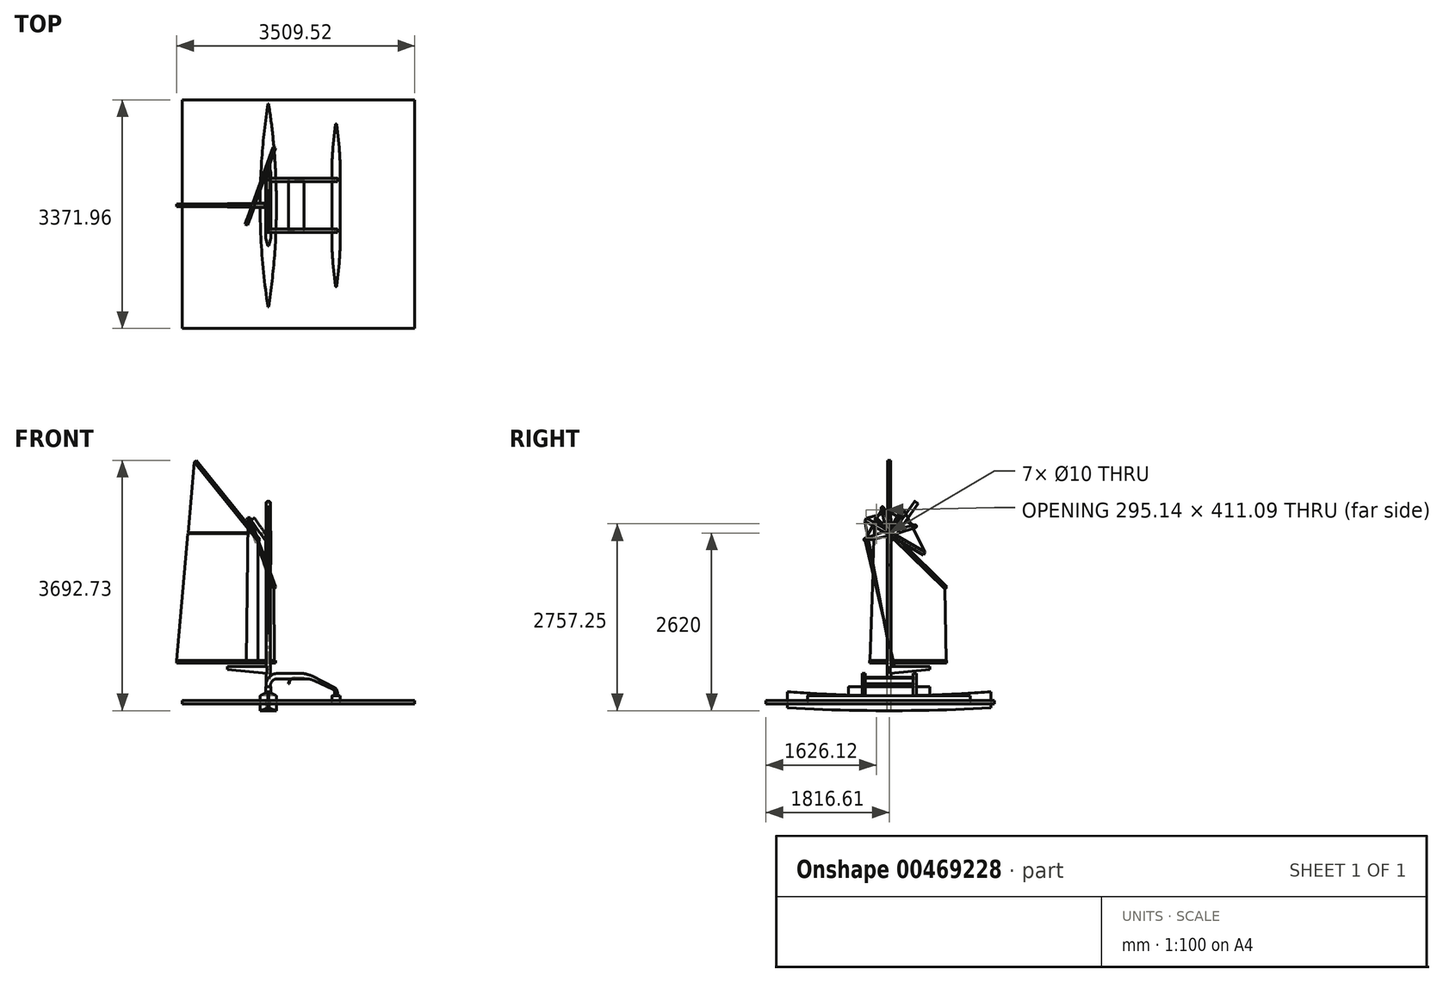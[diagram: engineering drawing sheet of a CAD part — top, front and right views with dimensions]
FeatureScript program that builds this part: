
annotation { "Feature Type Name" : "Feature", "Feature Type Description" : "" }
export const myFeature = defineFeature(function(context is Context, id is Id, definition is map)
    precondition{}
    {
        {
            var Q0;
            Q0=qCreatedBy(makeId("Top.planeOp"),FACE);
            var sketch = newSketch(context, id + "F0", { "sketchPlane" : qUnion([Q0])});
            skLineSegment(sketch, "E0", {"start": v(0, 0) * mm, "end": v(0, 1500) * mm});
            skLineSegment(sketch, "E1", {"start": v(0, 0) * mm, "end": v(120, 0) * mm});
            skLineSegment(sketch, "E2", {"start": v(120, 0) * mm, "end": v(120, -200) * mm, "construction": true});
            skLineSegment(sketch, "E3", {"start": v(0, 1500) * mm, "end": v(5, 1500) * mm});
            skArc(sketch, "E4", {"start": v(120, 0) * mm, "mid": v(91.2, 752.2) * mm, "end": v(5, 1500) * mm});
            skSolve(sketch);
        }
        {
            var Q0;
            Q0=qSketchRegion(id+"F0",true);
            extrude(context, id + "F1", {"entities" : qUnion([Q0]), "depth" : 110 * mm});
        }
        {
            var Q0;
            Q0=qCreatedBy(makeId("Right.planeOp"),FACE);
            var sketch = newSketch(context, id + "F2", { "sketchPlane" : qUnion([Q0])});
            skLineSegment(sketch, "E5.0", {"start": v(0, 0) * mm, "end": v(1500, 0) * mm});
            skLineSegment(sketch, "E6", {"start": v(1500, 0) * mm, "end": v(1500, 40) * mm});
            skLineSegment(sketch, "E7", {"start": v(0, 0) * mm, "end": v(-216.61, 0) * mm, "construction": true});
            skArc(sketch, "E8", {"start": v(0, 0) * mm, "mid": v(750.27, 10) * mm, "end": v(1500, 40) * mm});
            skSolve(sketch);
        }
        {
            var Q0;
            Q0=qSketchRegion(id+"F2",true);
            extrude(context, id + "F3", {"entities" : qUnion([Q0]), "operationType" : NewBodyOperationType.REMOVE, "depth" : 200 * mm});
        }
        {
            var Q0;
            Q0=makeQuery(id+"F1.opExtrude","SWEPT_BODY",BODY,{"disambiguationData":[OSD([sQuery(id+"F0.wireOp",EDGE,"E0"),sQuery(id+"F0.wireOp",EDGE,"E1"),sQuery(id+"F0.wireOp",EDGE,"E3"),sQuery(id+"F0.wireOp",EDGE,"E4")])]});
            var Q1;
            Q1=makeQuery(id+"F1.opExtrude","CAP_FACE",FACE,{"disambiguationData":[OSD([sQuery(id+"F0.wireOp",EDGE,"E0"),sQuery(id+"F0.wireOp",EDGE,"E1"),sQuery(id+"F0.wireOp",EDGE,"E3"),sQuery(id+"F0.wireOp",EDGE,"E4")])],"isStart":false});
            mirror(context, id + "F4", {"operationType" : NewBodyOperationType.ADD, "entities" : qUnion([Q0]), "mirrorPlane" : qUnion([Q1])});
        }
        {
            var Q0;
            Q0=makeQuery(id+"F1.opExtrude","SWEPT_BODY",BODY,{"disambiguationData":[OSD([sQuery(id+"F0.wireOp",EDGE,"E0"),sQuery(id+"F0.wireOp",EDGE,"E1"),sQuery(id+"F0.wireOp",EDGE,"E3"),sQuery(id+"F0.wireOp",EDGE,"E4")])]});
            var Q1;
            Q1=qCreatedBy(makeId("Right.planeOp"),FACE);
            mirror(context, id + "F5", {"operationType" : NewBodyOperationType.ADD, "entities" : qUnion([Q0]), "mirrorPlane" : qUnion([Q1])});
        }
        {
            var Q0;
            Q0=makeQuery(id+"F1.opExtrude","SWEPT_BODY",BODY,{"disambiguationData":[OSD([sQuery(id+"F0.wireOp",EDGE,"E0"),sQuery(id+"F0.wireOp",EDGE,"E1"),sQuery(id+"F0.wireOp",EDGE,"E3"),sQuery(id+"F0.wireOp",EDGE,"E4")])]});
            var Q1;
            Q1=qCreatedBy(makeId("Front.planeOp"),FACE);
            mirror(context, id + "F6", {"operationType" : NewBodyOperationType.ADD, "entities" : qUnion([Q0]), "mirrorPlane" : qUnion([Q1])});
        }
        {
            var Q0;
            Q0=qCreatedBy(makeId("Right.planeOp"),FACE);
            var sketch = newSketch(context, id + "F7", { "sketchPlane" : qUnion([Q0])});
            skLineSegment(sketch, "E9", {"start": v(-1500, 180) * mm, "end": v(-1500, 280) * mm});
            skLineSegment(sketch, "E10", {"start": v(1500, 180) * mm, "end": v(1500, 280) * mm});
            skLineSegment(sketch, "E11", {"start": v(0, 0) * mm, "end": v(0, 220) * mm, "construction": true});
            skArc(sketch, "E12", {"start": v(-1500, 280) * mm, "mid": v(0, 220) * mm, "end": v(1500, 280) * mm});
            skLineSegment(sketch, "E13", {"start": v(-1500, 180) * mm, "end": v(1500, 180) * mm});
            skSolve(sketch);
        }
        {
            var Q0;
            Q0=qSketchRegion(id+"F7",true);
            extrude(context, id + "F8", {"entities" : qUnion([Q0]), "operationType" : NewBodyOperationType.ADD, "depth" : 200 * mm, "hasSecondDirection" : true, "secondDirectionOppositeDirection" : true, "secondDirectionDepth" : 200 * mm});
        }
        {
            var Q0;
            Q0=makeQuery(id+"F8.opExtrude","SWEPT_FACE",FACE,{"disambiguationData":[OSD([sQuery(id+"F7.wireOp",EDGE,"E13")])]});
            var sketch = newSketch(context, id + "F9", { "sketchPlane" : qUnion([Q0])});
            skLineSegment(sketch, "E14.0", {"start": v(200, 1500) * mm, "end": v(200, -1500) * mm});
            skLineSegment(sketch, "E15.0", {"start": v(5, -1500) * mm, "end": v(-5, -1500) * mm});
            skLineSegment(sketch, "E16.0", {"start": v(-200, 1500) * mm, "end": v(-200, -1500) * mm});
            skArc(sketch, "E17.0", {"start": v(5, -1500) * mm, "mid": v(120, 0) * mm, "end": v(5, 1500) * mm});
            skArc(sketch, "E18.0", {"start": v(-5, 1500) * mm, "mid": v(-120, 0) * mm, "end": v(-5, -1500) * mm});
            skLineSegment(sketch, "E19.0", {"start": v(5, 1500) * mm, "end": v(-5, 1500) * mm});
            skLineSegment(sketch, "E20", {"start": v(-200, 1500) * mm, "end": v(-200, 1658.3) * mm});
            skLineSegment(sketch, "E21", {"start": v(-200, 1658.3) * mm, "end": v(200, 1658.3) * mm});
            skLineSegment(sketch, "E22", {"start": v(200, 1500) * mm, "end": v(200, 1658.3) * mm});
            skPoint(sketch, "E23.orphan", {"position": v(211.73, 1658.3) * mm});
            skLineSegment(sketch, "E24", {"start": v(-200, -1500) * mm, "end": v(-200, -1609.33) * mm});
            skLineSegment(sketch, "E25", {"start": v(200, -1500) * mm, "end": v(200, -1609.33) * mm});
            skLineSegment(sketch, "E26", {"start": v(-200, -1609.33) * mm, "end": v(200, -1609.33) * mm});
            skSolve(sketch);
        }
        {
            var Q0;
            Q0=qSketchRegion(id+"F9",true);
            extrude(context, id + "F10", {"entities" : qUnion([Q0]), "operationType" : NewBodyOperationType.REMOVE, "oppositeDirection" : true, "depth" : 200 * mm});
        }
        {
            var Q0;
            Q0=qCreatedBy(makeId("Top.planeOp"),FACE);
            cPlane(context, id + "F11", {"entities" : qUnion([Q0]), "cplaneType" : CPlaneType.OFFSET, "offset" : 100 * mm, "width" : 150 * mm, "height" : 150 * mm});
        }
        {
            var Q0;
            Q0=qCreatedBy(id+"F11.planeOp",FACE);
            var sketch = newSketch(context, id + "F12", { "sketchPlane" : qUnion([Q0])});
            skLineSegment(sketch, "E27.bottom", {"start": v(40, -600) * mm, "end": v(-40, -600) * mm});
            skLineSegment(sketch, "E27.top", {"start": v(40, 600) * mm, "end": v(-40, 600) * mm});
            skLineSegment(sketch, "E27.left", {"start": v(40, -600) * mm, "end": v(40, 600) * mm});
            skLineSegment(sketch, "E27.right", {"start": v(-40, -600) * mm, "end": v(-40, 600) * mm});
            skPoint(sketch, "E27.middle", {"position": v(0, 0) * mm});
            skSolve(sketch);
        }
        {
            var Q0;
            Q0=qSketchRegion(id+"F12",true);
            extrude(context, id + "F13", {"entities" : qUnion([Q0]), "operationType" : NewBodyOperationType.ADD, "depth" : 250 * mm});
        }
        {
            var Q0;
            Q0=makeQuery(id+"F13.opExtrude","SWEPT_EDGE",EDGE,{"disambiguationData":[OSD([sQuery(id+"F12.wireOp",EDGE,"E27.bottom"),sQuery(id+"F12.wireOp",EDGE,"E27.left")])]});
            var Q1;
            Q1=makeQuery(id+"F13.opExtrude","SWEPT_EDGE",EDGE,{"disambiguationData":[OSD([sQuery(id+"F12.wireOp",EDGE,"E27.bottom"),sQuery(id+"F12.wireOp",EDGE,"E27.right")])]});
            var Q2;
            Q2=makeQuery(id+"F13.opExtrude","SWEPT_EDGE",EDGE,{"disambiguationData":[OSD([sQuery(id+"F12.wireOp",EDGE,"E27.top"),sQuery(id+"F12.wireOp",EDGE,"E27.right")])]});
            var Q3;
            Q3=makeQuery(id+"F13.opExtrude","SWEPT_EDGE",EDGE,{"disambiguationData":[OSD([sQuery(id+"F12.wireOp",EDGE,"E27.top"),sQuery(id+"F12.wireOp",EDGE,"E27.left")])]});
            chamfer(context, id + "F14", {"entities" : qUnion([Q0, Q1, Q2, Q3]), "chamferType" : ChamferType.TWO_OFFSETS, "width1" : 35 * mm, "oppositeDirection" : true, "width2" : 120 * mm, "tangentPropagation" : true});
        }
        {
            var Q0;
            {var subQ0=sQuery(id+"F12.wireOp",EDGE,"E27.top");Q0=makeQuery(id+"F14.opChamfer","BLEND_EDGE",EDGE,{"blendedFrom":[makeQuery(id+"F13.opExtrude","SWEPT_EDGE",EDGE,{"disambiguationData":[OSD([subQ0,sQuery(id+"F12.wireOp",EDGE,"E27.right")])]}),makeQuery(id+"F13.opExtrude","SWEPT_FACE",FACE,{"disambiguationData":[OSD([subQ0])]})],"blendedInto":[makeQuery(id+"F13.opExtrude","SWEPT_FACE",FACE,{"disambiguationData":[OSD([subQ0])]})]});}
            var Q1;
            {var subQ0=sQuery(id+"F12.wireOp",EDGE,"E27.top");Q1=makeQuery(id+"F14.opChamfer","BLEND_EDGE",EDGE,{"blendedFrom":[makeQuery(id+"F13.opExtrude","SWEPT_EDGE",EDGE,{"disambiguationData":[OSD([subQ0,sQuery(id+"F12.wireOp",EDGE,"E27.left")])]}),makeQuery(id+"F13.opExtrude","SWEPT_FACE",FACE,{"disambiguationData":[OSD([subQ0])]})],"blendedInto":[makeQuery(id+"F13.opExtrude","SWEPT_FACE",FACE,{"disambiguationData":[OSD([subQ0])]})]});}
            var Q2;
            {var subQ0=sQuery(id+"F12.wireOp",EDGE,"E27.bottom");Q2=makeQuery(id+"F14.opChamfer","BLEND_EDGE",EDGE,{"blendedFrom":[makeQuery(id+"F13.opExtrude","SWEPT_EDGE",EDGE,{"disambiguationData":[OSD([subQ0,sQuery(id+"F12.wireOp",EDGE,"E27.right")])]}),makeQuery(id+"F13.opExtrude","SWEPT_FACE",FACE,{"disambiguationData":[OSD([subQ0])]})],"blendedInto":[makeQuery(id+"F13.opExtrude","SWEPT_FACE",FACE,{"disambiguationData":[OSD([subQ0])]})]});}
            var Q3;
            {var subQ0=sQuery(id+"F12.wireOp",EDGE,"E27.bottom");Q3=makeQuery(id+"F14.opChamfer","BLEND_EDGE",EDGE,{"blendedFrom":[makeQuery(id+"F13.opExtrude","SWEPT_EDGE",EDGE,{"disambiguationData":[OSD([subQ0,sQuery(id+"F12.wireOp",EDGE,"E27.left")])]}),makeQuery(id+"F13.opExtrude","SWEPT_FACE",FACE,{"disambiguationData":[OSD([subQ0])]})],"blendedInto":[makeQuery(id+"F13.opExtrude","SWEPT_FACE",FACE,{"disambiguationData":[OSD([subQ0])]})]});}
            fillet(context, id + "F15", {"entities" : qUnion([Q0, Q1, Q2, Q3]), "radius" : 5 * mm, "tangentPropagation" : true, "allowEdgeOverflow" : false});
        }
        {
            var Q0;
            {var subQ0=sQuery(id+"F12.wireOp",EDGE,"E27.right");Q0=makeQuery(id+"F14.opChamfer","BLEND_EDGE",EDGE,{"blendedFrom":[makeQuery(id+"F13.opExtrude","SWEPT_EDGE",EDGE,{"disambiguationData":[OSD([sQuery(id+"F12.wireOp",EDGE,"E27.bottom"),subQ0])]}),makeQuery(id+"F13.opExtrude","SWEPT_FACE",FACE,{"disambiguationData":[OSD([subQ0])]})],"blendedInto":[makeQuery(id+"F13.opExtrude","SWEPT_FACE",FACE,{"disambiguationData":[OSD([subQ0])]})]});}
            var Q1;
            {var subQ0=sQuery(id+"F12.wireOp",EDGE,"E27.left");Q1=makeQuery(id+"F14.opChamfer","BLEND_EDGE",EDGE,{"blendedFrom":[makeQuery(id+"F13.opExtrude","SWEPT_EDGE",EDGE,{"disambiguationData":[OSD([sQuery(id+"F12.wireOp",EDGE,"E27.bottom"),subQ0])]}),makeQuery(id+"F13.opExtrude","SWEPT_FACE",FACE,{"disambiguationData":[OSD([subQ0])]})],"blendedInto":[makeQuery(id+"F13.opExtrude","SWEPT_FACE",FACE,{"disambiguationData":[OSD([subQ0])]})]});}
            var Q2;
            {var subQ0=sQuery(id+"F12.wireOp",EDGE,"E27.left");Q2=makeQuery(id+"F14.opChamfer","BLEND_EDGE",EDGE,{"blendedFrom":[makeQuery(id+"F13.opExtrude","SWEPT_EDGE",EDGE,{"disambiguationData":[OSD([sQuery(id+"F12.wireOp",EDGE,"E27.top"),subQ0])]}),makeQuery(id+"F13.opExtrude","SWEPT_FACE",FACE,{"disambiguationData":[OSD([subQ0])]})],"blendedInto":[makeQuery(id+"F13.opExtrude","SWEPT_FACE",FACE,{"disambiguationData":[OSD([subQ0])]})]});}
            var Q3;
            {var subQ0=sQuery(id+"F12.wireOp",EDGE,"E27.right");Q3=makeQuery(id+"F14.opChamfer","BLEND_EDGE",EDGE,{"blendedFrom":[makeQuery(id+"F13.opExtrude","SWEPT_EDGE",EDGE,{"disambiguationData":[OSD([sQuery(id+"F12.wireOp",EDGE,"E27.top"),subQ0])]}),makeQuery(id+"F13.opExtrude","SWEPT_FACE",FACE,{"disambiguationData":[OSD([subQ0])]})],"blendedInto":[makeQuery(id+"F13.opExtrude","SWEPT_FACE",FACE,{"disambiguationData":[OSD([subQ0])]})]});}
            fillet(context, id + "F16", {"entities" : qUnion([Q0, Q1, Q2, Q3]), "radius" : 200 * mm, "tangentPropagation" : true, "allowEdgeOverflow" : false});
        }
        {
            var Q0;
            Q0=qCreatedBy(id+"F11.planeOp",FACE);
            var sketch = newSketch(context, id + "F17", { "sketchPlane" : qUnion([Q0])});
            skLineSegment(sketch, "E28.bottom", {"start": v(1060, 1200) * mm, "end": v(940, 1200) * mm});
            skLineSegment(sketch, "E28.top", {"start": v(1060, -1200) * mm, "end": v(940, -1200) * mm});
            skLineSegment(sketch, "E28.left", {"start": v(1060, 1200) * mm, "end": v(1060, -1200) * mm});
            skLineSegment(sketch, "E28.right", {"start": v(940, 1200) * mm, "end": v(940, -1200) * mm});
            skPoint(sketch, "E28.middle", {"position": v(1000, 0) * mm});
            skSolve(sketch);
        }
        {
            var Q0;
            Q0=qSketchRegion(id+"F17",true);
            extrude(context, id + "F18", {"entities" : qUnion([Q0]), "depth" : 120 * mm});
        }
        {
            var Q0;
            Q0=makeQuery(id+"F18.opExtrude","SWEPT_EDGE",EDGE,{"disambiguationData":[OSD([sQuery(id+"F17.wireOp",EDGE,"E28.top"),sQuery(id+"F17.wireOp",EDGE,"E28.right")])]});
            var Q1;
            Q1=makeQuery(id+"F18.opExtrude","SWEPT_EDGE",EDGE,{"disambiguationData":[OSD([sQuery(id+"F17.wireOp",EDGE,"E28.top"),sQuery(id+"F17.wireOp",EDGE,"E28.left")])]});
            var Q2;
            Q2=makeQuery(id+"F18.opExtrude","SWEPT_EDGE",EDGE,{"disambiguationData":[OSD([sQuery(id+"F17.wireOp",EDGE,"E28.bottom"),sQuery(id+"F17.wireOp",EDGE,"E28.right")])]});
            var Q3;
            Q3=makeQuery(id+"F18.opExtrude","SWEPT_EDGE",EDGE,{"disambiguationData":[OSD([sQuery(id+"F17.wireOp",EDGE,"E28.bottom"),sQuery(id+"F17.wireOp",EDGE,"E28.left")])]});
            chamfer(context, id + "F19", {"entities" : qUnion([Q0, Q1, Q2, Q3]), "chamferType" : ChamferType.TWO_OFFSETS, "width1" : 50 * mm, "oppositeDirection" : false, "width2" : 500 * mm, "tangentPropagation" : true});
        }
        {
            var Q0;
            {var subQ0=sQuery(id+"F17.wireOp",EDGE,"E28.top");Q0=makeQuery(id+"F19.opChamfer","BLEND_EDGE",EDGE,{"blendedFrom":[makeQuery(id+"F18.opExtrude","SWEPT_EDGE",EDGE,{"disambiguationData":[OSD([subQ0,sQuery(id+"F17.wireOp",EDGE,"E28.right")])]}),makeQuery(id+"F18.opExtrude","SWEPT_FACE",FACE,{"disambiguationData":[OSD([subQ0])]})],"blendedInto":[makeQuery(id+"F18.opExtrude","SWEPT_FACE",FACE,{"disambiguationData":[OSD([subQ0])]})]});}
            var Q1;
            {var subQ0=sQuery(id+"F17.wireOp",EDGE,"E28.top");Q1=makeQuery(id+"F19.opChamfer","BLEND_EDGE",EDGE,{"blendedFrom":[makeQuery(id+"F18.opExtrude","SWEPT_EDGE",EDGE,{"disambiguationData":[OSD([subQ0,sQuery(id+"F17.wireOp",EDGE,"E28.left")])]}),makeQuery(id+"F18.opExtrude","SWEPT_FACE",FACE,{"disambiguationData":[OSD([subQ0])]})],"blendedInto":[makeQuery(id+"F18.opExtrude","SWEPT_FACE",FACE,{"disambiguationData":[OSD([subQ0])]})]});}
            var Q2;
            {var subQ0=sQuery(id+"F17.wireOp",EDGE,"E28.bottom");Q2=makeQuery(id+"F19.opChamfer","BLEND_EDGE",EDGE,{"blendedFrom":[makeQuery(id+"F18.opExtrude","SWEPT_EDGE",EDGE,{"disambiguationData":[OSD([subQ0,sQuery(id+"F17.wireOp",EDGE,"E28.right")])]}),makeQuery(id+"F18.opExtrude","SWEPT_FACE",FACE,{"disambiguationData":[OSD([subQ0])]})],"blendedInto":[makeQuery(id+"F18.opExtrude","SWEPT_FACE",FACE,{"disambiguationData":[OSD([subQ0])]})]});}
            var Q3;
            {var subQ0=sQuery(id+"F17.wireOp",EDGE,"E28.bottom");Q3=makeQuery(id+"F19.opChamfer","BLEND_EDGE",EDGE,{"blendedFrom":[makeQuery(id+"F18.opExtrude","SWEPT_EDGE",EDGE,{"disambiguationData":[OSD([subQ0,sQuery(id+"F17.wireOp",EDGE,"E28.left")])]}),makeQuery(id+"F18.opExtrude","SWEPT_FACE",FACE,{"disambiguationData":[OSD([subQ0])]})],"blendedInto":[makeQuery(id+"F18.opExtrude","SWEPT_FACE",FACE,{"disambiguationData":[OSD([subQ0])]})]});}
            fillet(context, id + "F20", {"entities" : qUnion([Q0, Q1, Q2, Q3]), "radius" : 10 * mm, "tangentPropagation" : true, "allowEdgeOverflow" : false});
        }
        {
            var Q0;
            {var subQ0=sQuery(id+"F17.wireOp",EDGE,"E28.left");Q0=makeQuery(id+"F19.opChamfer","BLEND_EDGE",EDGE,{"blendedFrom":[makeQuery(id+"F18.opExtrude","SWEPT_EDGE",EDGE,{"disambiguationData":[OSD([sQuery(id+"F17.wireOp",EDGE,"E28.bottom"),subQ0])]}),makeQuery(id+"F18.opExtrude","SWEPT_FACE",FACE,{"disambiguationData":[OSD([subQ0])]})],"blendedInto":[makeQuery(id+"F18.opExtrude","SWEPT_FACE",FACE,{"disambiguationData":[OSD([subQ0])]})]});}
            var Q1;
            {var subQ0=sQuery(id+"F17.wireOp",EDGE,"E28.right");Q1=makeQuery(id+"F19.opChamfer","BLEND_EDGE",EDGE,{"blendedFrom":[makeQuery(id+"F18.opExtrude","SWEPT_EDGE",EDGE,{"disambiguationData":[OSD([sQuery(id+"F17.wireOp",EDGE,"E28.bottom"),subQ0])]}),makeQuery(id+"F18.opExtrude","SWEPT_FACE",FACE,{"disambiguationData":[OSD([subQ0])]})],"blendedInto":[makeQuery(id+"F18.opExtrude","SWEPT_FACE",FACE,{"disambiguationData":[OSD([subQ0])]})]});}
            var Q2;
            {var subQ0=sQuery(id+"F17.wireOp",EDGE,"E28.right");Q2=makeQuery(id+"F19.opChamfer","BLEND_EDGE",EDGE,{"blendedFrom":[makeQuery(id+"F18.opExtrude","SWEPT_EDGE",EDGE,{"disambiguationData":[OSD([sQuery(id+"F17.wireOp",EDGE,"E28.top"),subQ0])]}),makeQuery(id+"F18.opExtrude","SWEPT_FACE",FACE,{"disambiguationData":[OSD([subQ0])]})],"blendedInto":[makeQuery(id+"F18.opExtrude","SWEPT_FACE",FACE,{"disambiguationData":[OSD([subQ0])]})]});}
            var Q3;
            {var subQ0=sQuery(id+"F17.wireOp",EDGE,"E28.left");Q3=makeQuery(id+"F19.opChamfer","BLEND_EDGE",EDGE,{"blendedFrom":[makeQuery(id+"F18.opExtrude","SWEPT_EDGE",EDGE,{"disambiguationData":[OSD([sQuery(id+"F17.wireOp",EDGE,"E28.top"),subQ0])]}),makeQuery(id+"F18.opExtrude","SWEPT_FACE",FACE,{"disambiguationData":[OSD([subQ0])]})],"blendedInto":[makeQuery(id+"F18.opExtrude","SWEPT_FACE",FACE,{"disambiguationData":[OSD([subQ0])]})]});}
            fillet(context, id + "F21", {"entities" : qUnion([Q0, Q1, Q2, Q3]), "radius" : 3000 * mm, "tangentPropagation" : true, "allowEdgeOverflow" : false});
        }
        {
            var Q0;
            Q0=qCreatedBy(makeId("Front.planeOp"),FACE);
            cPlane(context, id + "F22", {"entities" : qUnion([Q0]), "cplaneType" : CPlaneType.OFFSET, "offset" : 400 * mm, "width" : 150 * mm, "height" : 150 * mm});
        }
        {
            var Q0;
            Q0=qCreatedBy(id+"F22.planeOp",FACE);
            var sketch = newSketch(context, id + "F23", { "sketchPlane" : qUnion([Q0])});
            skLineSegment(sketch, "E29", {"start": v(33.27, 350) * mm, "end": v(-33.27, 350) * mm});
            skLineSegment(sketch, "E30", {"start": v(1020, 220) * mm, "end": v(980, 220) * mm});
            skLineSegment(sketch, "E31", {"start": v(-33.27, 350) * mm, "end": v(-33.27, 380) * mm});
            skLineSegment(sketch, "E32", {"start": v(136.73, 550) * mm, "end": v(475.83, 550) * mm});
            skLineSegment(sketch, "E33", {"start": v(33.27, 350) * mm, "end": v(33.27, 370) * mm});
            skLineSegment(sketch, "E34", {"start": v(980, 220) * mm, "end": v(980, 268.3) * mm});
            skLineSegment(sketch, "E35", {"start": v(1020, 220) * mm, "end": v(1020, 270.88) * mm});
            skPoint(sketch, "E36.orphan", {"position": v(1060, 220) * mm});
            skPoint(sketch, "E37.orphan", {"position": v(940, 220) * mm});
            skLineSegment(sketch, "E38", {"start": v(647.78, 508.87) * mm, "end": v(976.2, 342.23) * mm});
            skLineSegment(sketch, "E39", {"start": v(133.27, 470) * mm, "end": v(552.25, 470) * mm});
            skLineSegment(sketch, "E40", {"start": v(680.18, 441.35) * mm, "end": v(951.32, 313.52) * mm});
            skPoint(sketch, "E41.visualSharp", {"position": v(33.27, 470) * mm});
            skArc(sketch, "E41.filletArc", {"start": v(133.27, 470) * mm, "mid": v(62.56, 440.71) * mm, "end": v(33.27, 370) * mm});
            skPoint(sketch, "E42.visualSharp", {"position": v(-33.27, 550) * mm});
            skArc(sketch, "E42.filletArc", {"start": v(136.73, 550) * mm, "mid": v(16.52, 500.2) * mm, "end": v(-33.27, 380) * mm});
            skPoint(sketch, "E43.visualSharp", {"position": v(619.42, 470) * mm});
            skArc(sketch, "E43.filletArc", {"start": v(680.18, 441.35) * mm, "mid": v(617.8, 462.75) * mm, "end": v(552.25, 470) * mm});
            skPoint(sketch, "E44.visualSharp", {"position": v(566.73, 550) * mm});
            skArc(sketch, "E44.filletArc", {"start": v(647.78, 508.87) * mm, "mid": v(564.23, 539.57) * mm, "end": v(475.83, 550) * mm});
            skPoint(sketch, "E45.visualSharp", {"position": v(980, 300) * mm});
            skArc(sketch, "E45.filletArc", {"start": v(980, 268.3) * mm, "mid": v(972.23, 295.07) * mm, "end": v(951.32, 313.52) * mm});
            skPoint(sketch, "E46.visualSharp", {"position": v(1020, 320) * mm});
            skArc(sketch, "E46.filletArc", {"start": v(1020, 270.88) * mm, "mid": v(1008.18, 312.74) * mm, "end": v(976.2, 342.23) * mm});
            skSolve(sketch);
        }
        {
            var Q0;
            Q0=qSketchRegion(id+"F23",true);
            extrude(context, id + "F24", {"entities" : qUnion([Q0]), "oppositeDirection" : true, "depth" : 50 * mm});
        }
        {
            var Q0;
            Q0=makeQuery(id+"F24.opExtrude","SWEPT_BODY",BODY,{"disambiguationData":[OSD([sQuery(id+"F23.wireOp",EDGE,"E29"),sQuery(id+"F23.wireOp",EDGE,"E30"),sQuery(id+"F23.wireOp",EDGE,"E31"),sQuery(id+"F23.wireOp",EDGE,"E32"),sQuery(id+"F23.wireOp",EDGE,"E33"),sQuery(id+"F23.wireOp",EDGE,"E34"),sQuery(id+"F23.wireOp",EDGE,"E35"),sQuery(id+"F23.wireOp",EDGE,"E38"),sQuery(id+"F23.wireOp",EDGE,"E39"),sQuery(id+"F23.wireOp",EDGE,"E40"),sQuery(id+"F23.wireOp",EDGE,"E41.filletArc"),sQuery(id+"F23.wireOp",EDGE,"E42.filletArc"),sQuery(id+"F23.wireOp",EDGE,"E43.filletArc"),sQuery(id+"F23.wireOp",EDGE,"E44.filletArc"),sQuery(id+"F23.wireOp",EDGE,"E45.filletArc"),sQuery(id+"F23.wireOp",EDGE,"E46.filletArc")])]});
            var Q1;
            Q1=qCreatedBy(makeId("Front.planeOp"),FACE);
            mirror(context, id + "F25", {"entities" : qUnion([Q0]), "mirrorPlane" : qUnion([Q1])});
        }
        {
            var Q0;
            Q0=qCreatedBy(makeId("Front.planeOp"),FACE);
            var sketch = newSketch(context, id + "F26", { "sketchPlane" : qUnion([Q0])});
            skLineSegment(sketch, "E47", {"start": v(0, 0) * mm, "end": v(0, 2500) * mm});
            skLineSegment(sketch, "E48", {"start": v(0, 2500) * mm, "end": v(-229.43, 2827.66) * mm});
            skPoint(sketch, "E49.visualSharp", {"position": v(0, 2500) * mm});
            skSolve(sketch);
        }
        {
            var Q0;
            Q0=makeQuery(id+"F13.opExtrude","CAP_FACE",FACE,{"disambiguationData":[OSD([sQuery(id+"F12.wireOp",EDGE,"E27.bottom"),sQuery(id+"F12.wireOp",EDGE,"E27.top"),sQuery(id+"F12.wireOp",EDGE,"E27.left"),sQuery(id+"F12.wireOp",EDGE,"E27.right")])],"isStart":false});
            var sketch = newSketch(context, id + "F27", { "sketchPlane" : qUnion([Q0])});
            skCircle(sketch, "E50", {"center": v(0, 0) * mm, "radius": 30 * mm});
            skSolve(sketch);
        }
        {
            var Q0;
            Q0=qSketchRegion(id+"F27",true);
            var Q1;
            Q1=qBodyType(qCreatedBy(id+"F26",EDGE),BodyType.WIRE);
            sweep(context, id + "F28", {"profiles" : qUnion([Q0]), "path" : qUnion([Q1])});
        }
        {
            var Q0;
            Q0=qCreatedBy(makeId("Front.planeOp"),FACE);
            var sketch = newSketch(context, id + "F29", { "sketchPlane" : qUnion([Q0])});
            skLineSegment(sketch, "E51", {"start": v(-118.86, 2525.11) * mm, "end": v(-1060.5, 3692.73) * mm});
            skLineSegment(sketch, "E52", {"start": v(-1060.5, 3692.73) * mm, "end": v(-1091.63, 3667.62) * mm});
            skLineSegment(sketch, "E53", {"start": v(-1091.63, 3667.62) * mm, "end": v(-150, 2500) * mm});
            skLineSegment(sketch, "E54", {"start": v(-150, 2500) * mm, "end": v(-118.86, 2525.11) * mm});
            skPoint(sketch, "E55.orphan", {"position": v(508.89, 1746.7) * mm});
            skSolve(sketch);
        }
        {
            var Q0;
            Q0=qSketchRegion(id+"F29",true);
            extrude(context, id + "F30", {"entities" : qUnion([Q0]), "depth" : 20 * mm, "hasSecondDirection" : true, "secondDirectionOppositeDirection" : true, "secondDirectionDepth" : 20 * mm});
        }
        {
            var Q0;
            Q0=qCreatedBy(makeId("Front.planeOp"),FACE);
            var sketch = newSketch(context, id + "F31", { "sketchPlane" : qUnion([Q0])});
            skLineSegment(sketch, "E56", {"start": v(0, 650) * mm, "end": v(-600, 650) * mm});
            skLineSegment(sketch, "E57", {"start": v(-600, 650) * mm, "end": v(-600, 610) * mm});
            skLineSegment(sketch, "E58", {"start": v(-600, 610) * mm, "end": v(0, 550) * mm});
            skLineSegment(sketch, "E59", {"start": v(0, 650) * mm, "end": v(0, 550) * mm});
            skSolve(sketch);
        }
        {
            var Q0;
            Q0=qSketchRegion(id+"F31",true);
            extrude(context, id + "F32", {"entities" : qUnion([Q0]), "operationType" : NewBodyOperationType.ADD, "depth" : 25 * mm, "hasSecondDirection" : true, "secondDirectionOppositeDirection" : true, "secondDirectionDepth" : 25 * mm});
        }
        {
            var Q0;
            Q0=qCreatedBy(makeId("Front.planeOp"),FACE);
            var sketch = newSketch(context, id + "F33", { "sketchPlane" : qUnion([Q0])});
            skLineSegment(sketch, "E60.bottom", {"start": v(-150, 740) * mm, "end": v(-1350, 740) * mm});
            skLineSegment(sketch, "E60.top", {"start": v(-150, 700) * mm, "end": v(-1350, 700) * mm});
            skLineSegment(sketch, "E60.left", {"start": v(-150, 740) * mm, "end": v(-150, 700) * mm});
            skLineSegment(sketch, "E60.right", {"start": v(-1350, 740) * mm, "end": v(-1350, 700) * mm});
            skSolve(sketch);
        }
        {
            var Q0;
            Q0=qSketchRegion(id+"F33",true);
            extrude(context, id + "F34", {"entities" : qUnion([Q0]), "depth" : 20 * mm, "hasSecondDirection" : true, "secondDirectionOppositeDirection" : true, "secondDirectionDepth" : 20 * mm});
        }
        {
            var Q0;
            Q0=qCreatedBy(makeId("Front.planeOp"),FACE);
            var sketch = newSketch(context, id + "F35", { "sketchPlane" : qUnion([Q0])});
            skLineSegment(sketch, "E61.0", {"start": v(-1091.63, 3667.62) * mm, "end": v(-150, 2500) * mm});
            skLineSegment(sketch, "E62.0", {"start": v(-150, 740) * mm, "end": v(-1350, 740) * mm});
            skLineSegment(sketch, "E63", {"start": v(-150, 2500) * mm, "end": v(-150, 740) * mm});
            skLineSegment(sketch, "E64", {"start": v(-1091.63, 3667.62) * mm, "end": v(-1350, 740) * mm});
            skSolve(sketch);
        }
        {
            var Q0;
            Q0=qSketchRegion(id+"F35",true);
            extrude(context, id + "F36", {"entities" : qUnion([Q0]), "depth" : .2 * mm, "hasSecondDirection" : true, "secondDirectionOppositeDirection" : true, "secondDirectionDepth" : .2 * mm});
        }
        {
            var Q0;
            Q0=qCreatedBy(makeId("Front.planeOp"),FACE);
            var sketch = newSketch(context, id + "F37", { "sketchPlane" : qUnion([Q0])});
            skLineSegment(sketch, "E65.bottom", {"start": v(310, 480) * mm, "end": v(528.88, 480) * mm});
            skLineSegment(sketch, "E65.top", {"start": v(300, 490) * mm, "end": v(528.88, 490) * mm});
            skLineSegment(sketch, "E65.left", {"start": v(300, 480) * mm, "end": v(300, 490) * mm});
            skLineSegment(sketch, "E65.right", {"start": v(528.88, 480) * mm, "end": v(528.88, 490) * mm});
            skLineSegment(sketch, "E66", {"start": v(300, 480) * mm, "end": v(300, 397.55) * mm});
            skLineSegment(sketch, "E67", {"start": v(300, 397.55) * mm, "end": v(310, 397.55) * mm});
            skLineSegment(sketch, "E68", {"start": v(310, 397.55) * mm, "end": v(310, 480) * mm});
            skSolve(sketch);
        }
        {
            var Q0;
            Q0=qSketchRegion(id+"F37",true);
            extrude(context, id + "F38", {"entities" : qUnion([Q0]), "depth" : 390 * mm, "hasSecondDirection" : true, "secondDirectionOppositeDirection" : true, "secondDirectionDepth" : 390 * mm});
        }
        {
            var Q0;
            Q0=makeQuery(id+"F38.opExtrude","SWEPT_EDGE",EDGE,{"disambiguationData":[OSD([sQuery(id+"F37.wireOp",EDGE,"E65.bottom"),sQuery(id+"F37.wireOp",EDGE,"E68")])]});
            fillet(context, id + "F39", {"entities" : qUnion([Q0]), "radius" : 80 * mm, "tangentPropagation" : true, "allowEdgeOverflow" : false});
        }
        {
            var Q0;
            Q0=makeQuery(id+"F38.opExtrude","SWEPT_EDGE",EDGE,{"disambiguationData":[OSD([sQuery(id+"F37.wireOp",EDGE,"E65.top"),sQuery(id+"F37.wireOp",EDGE,"E65.left")])]});
            fillet(context, id + "F40", {"entities" : qUnion([Q0]), "radius" : 90 * mm, "tangentPropagation" : true, "allowEdgeOverflow" : false});
        }
        {
            var Q0;
            Q0=qCreatedBy(makeId("Right.planeOp"),FACE);
            var sketch = newSketch(context, id + "F41", { "sketchPlane" : qUnion([Q0])});
            skLineSegment(sketch, "E69", {"start": v(1440.24, 469.7) * mm, "end": v(-967.66, 1898.69) * mm, "construction": true});
            skLineSegment(sketch, "E70", {"start": v(816.57, 1770.1) * mm, "end": v(408.28, 1082.12) * mm, "construction": true});
            skLineSegment(sketch, "E71", {"start": v(408.28, 1082.12) * mm, "end": v(0, 394.15) * mm, "construction": true});
            skLineSegment(sketch, "E72", {"start": v(-459.32, 1597.01) * mm, "end": v(0, 2370.98) * mm, "construction": true});
            skLineSegment(sketch, "E73", {"start": v(-459.32, 1597.01) * mm, "end": v(-918.64, 823.04) * mm, "construction": true});
            skPoint(sketch, "E74", {"position": v(-279.69, 1490.4) * mm});
            skArc(sketch, "E75", {"start": v(1440.24, 469.7) * mm, "mid": v(957.4, 1600.08) * mm, "end": v(0, 2370.98) * mm});
            skArc(sketch, "E76", {"start": v(-918.64, 823.04) * mm, "mid": v(216.7, 351.98) * mm, "end": v(1440.24, 469.7) * mm});
            skLineSegment(sketch, "E77", {"start": v(0, 0) * mm, "end": v(2000, 0) * mm, "construction": true});
            skLineSegment(sketch, "E78", {"start": v(2000, 0) * mm, "end": v(1440.24, 469.7) * mm, "construction": true});
            skArc(sketch, "E79", {"start": v(-918.64, 823.04) * mm, "mid": v(-279.69, 1490.4) * mm, "end": v(0, 2370.98) * mm});
            skSolve(sketch);
        }
        {
            var Q0;
            Q0=qCreatedBy(makeId("Right.planeOp"),FACE);
            var sketch = newSketch(context, id + "F42", { "sketchPlane" : qUnion([Q0])});
            skLineSegment(sketch, "E80", {"start": v(0, 0) * mm, "end": v(0, 2500) * mm});
            skLineSegment(sketch, "E81", {"start": v(0, 2500) * mm, "end": v(401.5, 3073.4) * mm});
            skSolve(sketch);
        }
        {
            var Q0;
            Q0=qCreatedBy(makeId("Top.planeOp"),FACE);
            var sketch = newSketch(context, id + "F43", { "sketchPlane" : qUnion([Q0])});
            skCircle(sketch, "E82", {"center": v(0, 0) * mm, "radius": 30 * mm});
            skSolve(sketch);
        }
        {
            var Q0;
            Q0=qSketchRegion(id+"F43",true);
            var Q1;
            Q1=qBodyType(qCreatedBy(id+"F42",EDGE),BodyType.WIRE);
            sweep(context, id + "F44", {"profiles" : qUnion([Q0]), "path" : qUnion([Q1])});
        }
        {
            var Q0;
            Q0=qCreatedBy(makeId("Right.planeOp"),FACE);
            var sketch = newSketch(context, id + "F45", { "sketchPlane" : qUnion([Q0])});
            skLineSegment(sketch, "E83", {"start": v(0, 650) * mm, "end": v(600, 650) * mm});
            skLineSegment(sketch, "E84", {"start": v(600, 650) * mm, "end": v(600, 610) * mm});
            skLineSegment(sketch, "E85", {"start": v(600, 610) * mm, "end": v(0, 550) * mm});
            skLineSegment(sketch, "E86", {"start": v(0, 550) * mm, "end": v(0, 650) * mm});
            skSolve(sketch);
        }
        {
            var Q0;
            Q0=qSketchRegion(id+"F45",true);
            extrude(context, id + "F46", {"entities" : qUnion([Q0]), "operationType" : NewBodyOperationType.ADD, "depth" : 25 * mm, "hasSecondDirection" : true, "secondDirectionOppositeDirection" : true, "secondDirectionDepth" : 25 * mm});
        }
        {
            var Q0;
            Q0=makeQuery(id+"F46.opExtrude","CAP_FACE",FACE,{"disambiguationData":[OSD([sQuery(id+"F45.wireOp",EDGE,"E83"),sQuery(id+"F45.wireOp",EDGE,"E84"),sQuery(id+"F45.wireOp",EDGE,"E85"),sQuery(id+"F45.wireOp",EDGE,"E86")])],"isStart":false});
            cPlane(context, id + "F47", {"entities" : qUnion([Q0]), "cplaneType" : CPlaneType.OFFSET, "offset" : 25 * mm, "width" : 150 * mm, "height" : 150 * mm});
        }
        {
            var Q0;
            Q0=qCreatedBy(id+"F47.planeOp",FACE);
            var Q1;
            Q1=makeQuery(id+"F46.opExtrude","CAP_EDGE",EDGE,{"disambiguationData":[OSD([sQuery(id+"F45.wireOp",EDGE,"E84")])],"isStart":false});
            cPlane(context, id + "F48", {"entities" : qUnion([Q0, Q1]), "cplaneType" : CPlaneType.LINE_ANGLE, "offset" : 25 * mm, "angle" : 20 * degree, "width" : 150 * mm, "height" : 150 * mm});
        }
        {
            var Q0;
            Q0=qCreatedBy(id+"F48.planeOp",FACE);
            cPlane(context, id + "F49", {"entities" : qUnion([Q0]), "cplaneType" : CPlaneType.OFFSET, "offset" : 25 * mm, "width" : 150 * mm, "height" : 150 * mm});
        }
        {
            var Q0;
            Q0=qCreatedBy(id+"F49.planeOp",FACE);
            var sketch = newSketch(context, id + "F50", { "sketchPlane" : qUnion([Q0])});
            skLineSegment(sketch, "E87.bottom", {"start": v(377.63, 740) * mm, "end": v(-822.37, 740) * mm});
            skLineSegment(sketch, "E87.top", {"start": v(377.63, 700) * mm, "end": v(-822.37, 700) * mm});
            skLineSegment(sketch, "E87.left", {"start": v(377.63, 740) * mm, "end": v(377.63, 700) * mm});
            skLineSegment(sketch, "E87.right", {"start": v(-822.37, 740) * mm, "end": v(-822.37, 700) * mm});
            skSolve(sketch);
        }
        {
            var Q0;
            Q0=qSketchRegion(id+"F50",true);
            extrude(context, id + "F51", {"entities" : qUnion([Q0]), "depth" : 20 * mm, "hasSecondDirection" : true, "secondDirectionOppositeDirection" : true, "secondDirectionDepth" : 20 * mm});
        }
        {
            var Q0;
            Q0=qCreatedBy(id+"F49.planeOp",FACE);
            var sketch = newSketch(context, id + "F52", { "sketchPlane" : qUnion([Q0])});
            skLineSegment(sketch, "E88", {"start": v(-827.14, 1829.38) * mm, "end": v(274.74, 2847.16) * mm});
            skLineSegment(sketch, "E89", {"start": v(274.74, 2847.16) * mm, "end": v(-827.14, 1829.38) * mm});
            skLineSegment(sketch, "E90.0", {"start": v(301.88, 2817.78) * mm, "end": v(-800, 1800) * mm});
            skLineSegment(sketch, "E91", {"start": v(-800, 1800) * mm, "end": v(-827.14, 1829.38) * mm});
            skLineSegment(sketch, "E92", {"start": v(301.88, 2817.78) * mm, "end": v(274.74, 2847.16) * mm});
            skSolve(sketch);
        }
        {
            var Q0;
            Q0=qSketchRegion(id+"F52",true);
            extrude(context, id + "F53", {"entities" : qUnion([Q0]), "depth" : 20 * mm, "hasSecondDirection" : true, "secondDirectionOppositeDirection" : true, "secondDirectionDepth" : 20 * mm});
        }
        {
            var Q0;
            Q0=makeQuery(id+"F51.opExtrude","CAP_FACE",FACE,{"disambiguationData":[OSD([sQuery(id+"F50.wireOp",EDGE,"E87.bottom"),sQuery(id+"F50.wireOp",EDGE,"E87.top"),sQuery(id+"F50.wireOp",EDGE,"E87.left"),sQuery(id+"F50.wireOp",EDGE,"E87.right")])],"isStart":true});
            cPlane(context, id + "F54", {"entities" : qUnion([Q0]), "cplaneType" : CPlaneType.OFFSET, "offset" : 20 * mm, "oppositeDirection" : true, "width" : 150 * mm, "height" : 150 * mm});
        }
        {
            var Q0;
            Q0=qCreatedBy(id+"F54.planeOp",FACE);
            var sketch = newSketch(context, id + "F55", { "sketchPlane" : qUnion([Q0])});
            skLineSegment(sketch, "E93.0", {"start": v(-377.63, 740) * mm, "end": v(822.37, 740) * mm});
            skLineSegment(sketch, "E94.0", {"start": v(-301.88, 2817.78) * mm, "end": v(800, 1800) * mm});
            skLineSegment(sketch, "E95", {"start": v(800, 1800) * mm, "end": v(822.37, 740) * mm});
            skLineSegment(sketch, "E96", {"start": v(-301.88, 2817.78) * mm, "end": v(-377.63, 740) * mm});
            skSolve(sketch);
        }
        {
            var Q0;
            Q0=qSketchRegion(id+"F55",true);
            extrude(context, id + "F56", {"entities" : qUnion([Q0]), "depth" : 1 * mm});
        }
        {
            var Q0;
            Q0=qCreatedBy(id+"F11.planeOp",FACE);
            var sketch = newSketch(context, id + "F57", { "sketchPlane" : qUnion([Q0])});
            skLineSegment(sketch, "E97.bottom", {"start": v(-1270, -1816.61) * mm, "end": v(2159.52, -1816.61) * mm});
            skLineSegment(sketch, "E97.top", {"start": v(-1270, 1555.35) * mm, "end": v(2159.52, 1555.35) * mm});
            skLineSegment(sketch, "E97.left", {"start": v(-1270, -1816.61) * mm, "end": v(-1270, 1555.35) * mm});
            skLineSegment(sketch, "E97.right", {"start": v(2159.52, -1816.61) * mm, "end": v(2159.52, 1555.35) * mm});
            skSolve(sketch);
        }
        {
            var Q0;
            Q0=qSketchRegion(id+"F57",true);
            extrude(context, id + "F58", {"entities" : qUnion([Q0]), "depth" : 50 * mm});
        }
        {
            var Q0;
            Q0=qSketchRegion(id+"F27",true);
            extrude(context, id + "F59", {"entities" : qUnion([Q0]), "depth" : 1800 * mm});
        }
        {
            var Q0;
            Q0=makeQuery(id+"F59.opExtrude","CAP_FACE",FACE,{"disambiguationData":[OSD([sQuery(id+"F27.wireOp",EDGE,"E50")])],"isStart":false});
            var sketch = newSketch(context, id + "F60", { "sketchPlane" : qUnion([Q0])});
            skLineSegment(sketch, "E98.bottom", {"start": v(40, 30) * mm, "end": v(-40, 30) * mm});
            skLineSegment(sketch, "E98.top", {"start": v(40, -30) * mm, "end": v(-40, -30) * mm});
            skLineSegment(sketch, "E98.left", {"start": v(40, 30) * mm, "end": v(40, -30) * mm});
            skLineSegment(sketch, "E98.right", {"start": v(-40, 30) * mm, "end": v(-40, -30) * mm});
            skPoint(sketch, "E98.middle", {"position": v(0, 0) * mm});
            skSolve(sketch);
        }
        {
            var Q0;
            Q0=qSketchRegion(id+"F60",true);
            extrude(context, id + "F61", {"entities" : qUnion([Q0]), "operationType" : NewBodyOperationType.ADD, "depth" : 500 * mm});
        }
        {
            var Q0;
            Q0=makeQuery(id+"F61.opExtrude","SWEPT_FACE",FACE,{"disambiguationData":[OSD([sQuery(id+"F60.wireOp",EDGE,"E98.top")])]});
            var sketch = newSketch(context, id + "F62", { "sketchPlane" : qUnion([Q0])});
            skLineSegment(sketch, "E99.bottom", {"start": v(-10, 2350) * mm, "end": v(10, 2350) * mm});
            skLineSegment(sketch, "E99.top", {"start": v(-10, 2655) * mm, "end": v(10, 2655) * mm});
            skLineSegment(sketch, "E99.left", {"start": v(-10, 2350) * mm, "end": v(-10, 2655) * mm});
            skLineSegment(sketch, "E99.right", {"start": v(10, 2350) * mm, "end": v(10, 2655) * mm});
            skSolve(sketch);
        }
        {
            var Q0;
            Q0=qSketchRegion(id+"F62",true);
            extrude(context, id + "F63", {"entities" : qUnion([Q0]), "operationType" : NewBodyOperationType.REMOVE, "oppositeDirection" : true, "depth" : 100 * mm});
        }
        {
            var Q0;
            Q0=makeQuery(id+"F61.opExtrude","SWEPT_FACE",FACE,{"disambiguationData":[OSD([sQuery(id+"F60.wireOp",EDGE,"E98.left")])]});
            var sketch = newSketch(context, id + "F64", { "sketchPlane" : qUnion([Q0])});
            skCircle(sketch, "E100", {"center": v(0, 2620) * mm, "radius": 5 * mm});
            skSolve(sketch);
        }
        {
            var Q0;
            Q0=qSketchRegion(id+"F64",true);
            extrude(context, id + "F65", {"entities" : qUnion([Q0]), "operationType" : NewBodyOperationType.REMOVE, "endBound" : BoundingType.THROUGH_ALL, "oppositeDirection" : true, "depth" : 25 * mm});
        }
        {
            var Q0;
            Q0=qCreatedBy(makeId("Right.planeOp"),FACE);
            var sketch = newSketch(context, id + "F66", { "sketchPlane" : qUnion([Q0])});
            skCircle(sketch, "E101.0", {"center": v(0, 2620) * mm, "radius": 5 * mm});
            skArc(sketch, "E102", {"start": v(8.19, 2580.85) * mm, "mid": v(10.23, 2581.33) * mm, "end": v(12.25, 2581.92) * mm});
            skLineSegment(sketch, "E103", {"start": v(384.16, 2722.54) * mm, "end": v(-353.44, 2525.66) * mm, "construction": true});
            skPoint(sketch, "E104.orphan", {"position": v(0, 3303.42) * mm});
            skLineSegment(sketch, "E105", {"start": v(0, 2620) * mm, "end": v(-99, 2990.88) * mm, "construction": true});
            skArc(sketch, "E106", {"start": v(-79.97, 2997.04) * mm, "mid": v(-104.33, 3010.16) * mm, "end": v(-118.48, 2986.38) * mm});
            skArc(sketch, "E107", {"start": v(-359.63, 2544.68) * mm, "mid": v(-372.89, 2521) * mm, "end": v(-350.33, 2505.9) * mm});
            skLineSegment(sketch, "E108", {"start": v(-359.63, 2544.68) * mm, "end": v(-340.83, 2550.8) * mm});
            skLineSegment(sketch, "E109", {"start": v(-348.37, 2506.29) * mm, "end": v(8.19, 2580.85) * mm});
            skLineSegment(sketch, "E110", {"start": v(-118.55, 2986.67) * mm, "end": v(-113.88, 2965.75) * mm});
            skLineSegment(sketch, "E111", {"start": v(-79.97, 2997.04) * mm, "end": v(-73.82, 2978.04) * mm});
            skLineSegment(sketch, "E112", {"start": v(26.94, 2666.66) * mm, "end": v(356.08, 2737) * mm});
            skLineSegment(sketch, "E113", {"start": v(12.25, 2581.92) * mm, "end": v(390.28, 2703.5) * mm});
            skLineSegment(sketch, "E114", {"start": v(-99, 2990.88) * mm, "end": v(384.16, 2722.54) * mm, "construction": true});
            skLineSegment(sketch, "E115", {"start": v(-353.44, 2525.66) * mm, "end": v(-99, 2990.88) * mm, "construction": true});
            skLineSegment(sketch, "E116.0", {"start": v(-99.48, 2990) * mm, "end": v(-99.48, 2990) * mm});
            skLineSegment(sketch, "E117.0", {"start": v(-73.82, 2978.04) * mm, "end": v(359.05, 2737.63) * mm});
            skLineSegment(sketch, "E118.trimOffspring", {"start": v(-72.92, 2975.25) * mm, "end": v(26.94, 2666.66) * mm});
            skLineSegment(sketch, "E119.trimOffspring", {"start": v(-72.92, 2975.25) * mm, "end": v(356.08, 2737) * mm});
            skLineSegment(sketch, "E120.trimOffspring", {"start": v(-113.22, 2962.8) * mm, "end": v(-42.91, 2647.8) * mm});
            skLineSegment(sketch, "E121.trimOffspring", {"start": v(-98.62, 2989.48) * mm, "end": v(-98.6, 2989.52) * mm});
            skLineSegment(sketch, "E122.trimOffspring", {"start": v(-98.12, 2990.4) * mm, "end": v(-98.12, 2990.4) * mm});
            skLineSegment(sketch, "E123.trimOffspring", {"start": v(-98.64, 2989.54) * mm, "end": v(-98.6, 2989.52) * mm});
            skLineSegment(sketch, "E124.trimOffspring", {"start": v(-338.06, 2551.7) * mm, "end": v(-42.91, 2647.8) * mm});
            skLineSegment(sketch, "E125.trimOffspring", {"start": v(-338.06, 2551.7) * mm, "end": v(-113.22, 2962.8) * mm});
            skLineSegment(sketch, "E126.trimOffspring", {"start": v(-340.83, 2550.8) * mm, "end": v(-113.88, 2965.75) * mm});
            skArc(sketch, "E127.trimOffspring", {"start": v(390.28, 2703.5) * mm, "mid": v(403.48, 2727.7) * mm, "end": v(379.98, 2742.1) * mm});
            skLineSegment(sketch, "E128.trimOffspring", {"start": v(359.05, 2737.63) * mm, "end": v(379.98, 2742.1) * mm});
            skLineSegment(sketch, "E129", {"start": v(-349.35, 2506.08) * mm, "end": v(0, 1000) * mm, "construction": true});
            skLineSegment(sketch, "E130.0", {"start": v(-350.33, 2505.9) * mm, "end": v(87.55, 618.14) * mm});
            skLineSegment(sketch, "E131.0", {"start": v(-348.37, 2506.29) * mm, "end": v(89.52, 618.5) * mm});
            skLineSegment(sketch, "E132", {"start": v(89.52, 618.5) * mm, "end": v(87.55, 618.14) * mm});
            skSolve(sketch);
        }
        {
            var Q0;
            Q0=qSketchRegion(id+"F66",true);
            extrude(context, id + "F67", {"entities" : qUnion([Q0]), "depth" : 1 * mm, "hasSecondDirection" : true, "secondDirectionOppositeDirection" : true, "secondDirectionDepth" : 1 * mm});
        }
        {
            var Q0;
            Q0=makeQuery(id+"F61.opExtrude","SWEPT_EDGE",EDGE,{"disambiguationData":[OSD([sQuery(id+"F60.wireOp",EDGE,"E98.bottom"),sQuery(id+"F60.wireOp",EDGE,"E98.left")])]});
            var Q1;
            Q1=makeQuery(id+"F61.opExtrude","SWEPT_EDGE",EDGE,{"disambiguationData":[OSD([sQuery(id+"F60.wireOp",EDGE,"E98.top"),sQuery(id+"F60.wireOp",EDGE,"E98.left")])]});
            var Q2;
            Q2=makeQuery(id+"F61.opExtrude","SWEPT_EDGE",EDGE,{"disambiguationData":[OSD([sQuery(id+"F60.wireOp",EDGE,"E98.top"),sQuery(id+"F60.wireOp",EDGE,"E98.right")])]});
            var Q3;
            Q3=makeQuery(id+"F61.opExtrude","SWEPT_EDGE",EDGE,{"disambiguationData":[OSD([sQuery(id+"F60.wireOp",EDGE,"E98.bottom"),sQuery(id+"F60.wireOp",EDGE,"E98.right")])]});
            var Q4;
            Q4=makeQuery(id+"F61.opExtrude","CAP_EDGE",EDGE,{"disambiguationData":[OSD([sQuery(id+"F60.wireOp",EDGE,"E98.right")])],"isStart":true});
            var Q5;
            Q5=makeQuery(id+"F61.opExtrude","CAP_EDGE",EDGE,{"disambiguationData":[OSD([sQuery(id+"F60.wireOp",EDGE,"E98.left")])],"isStart":true});
            fillet(context, id + "F68", {"entities" : qUnion([Q0, Q1, Q2, Q3, Q4, Q5]), "radius" : 20 * mm, "tangentPropagation" : true, "allowEdgeOverflow" : false});
        }
        {
            var Q0;
            Q0=qCreatedBy(makeId("Right.planeOp"),FACE);
            var sketch = newSketch(context, id + "F69", { "sketchPlane" : qUnion([Q0])});
            skLineSegment(sketch, "E133", {"start": v(600, 650) * mm, "end": v(0, 650) * mm});
            skLineSegment(sketch, "E134", {"start": v(0, 650) * mm, "end": v(0, 550) * mm});
            skLineSegment(sketch, "E135", {"start": v(0, 550) * mm, "end": v(600, 610) * mm});
            skLineSegment(sketch, "E136", {"start": v(600, 610) * mm, "end": v(600, 650) * mm});
            skSolve(sketch);
        }
        {
            var Q0;
            Q0=qSketchRegion(id+"F69",true);
            extrude(context, id + "F70", {"entities" : qUnion([Q0]), "operationType" : NewBodyOperationType.ADD, "depth" : 25 * mm, "hasSecondDirection" : true, "secondDirectionOppositeDirection" : true, "secondDirectionDepth" : 25 * mm});
        }
        {
            var Q0;
            Q0=qCreatedBy(makeId("Right.planeOp"),FACE);
            var sketch = newSketch(context, id + "F71", { "sketchPlane" : qUnion([Q0])});
            skLineSegment(sketch, "E137", {"start": v(-358.23, 2797.96) * mm, "end": v(506.66, 2298.6) * mm});
            skLineSegment(sketch, "E138", {"start": v(506.66, 2298.6) * mm, "end": v(531.66, 2341.91) * mm});
            skLineSegment(sketch, "E139", {"start": v(531.66, 2341.91) * mm, "end": v(29.82, 2631.65) * mm});
            skLineSegment(sketch, "E140", {"start": v(-358.23, 2797.96) * mm, "end": v(-333.23, 2841.26) * mm});
            skCircle(sketch, "E141.0", {"center": v(0, 2620) * mm, "radius": 5 * mm});
            skLineSegment(sketch, "E142", {"start": v(0, 2620) * mm, "end": v(0, 2403.95) * mm, "construction": true});
            skLineSegment(sketch, "E143", {"start": v(0, 2620) * mm, "end": v(221.24, 3003.2) * mm, "construction": true});
            skLineSegment(sketch, "E144.0", {"start": v(29.82, 2631.65) * mm, "end": v(217.07, 2955.98) * mm});
            skLineSegment(sketch, "E145.0", {"start": v(-4.82, 2651.65) * mm, "end": v(182.43, 2975.98) * mm});
            skLineSegment(sketch, "E146", {"start": v(182.43, 2975.98) * mm, "end": v(217.07, 2955.98) * mm});
            skLineSegment(sketch, "E147.trimOffspring", {"start": v(-4.82, 2651.65) * mm, "end": v(-333.23, 2841.26) * mm});
            skLineSegment(sketch, "E148", {"start": v(-4.82, 2651.65) * mm, "end": v(29.82, 2631.65) * mm, "construction": true});
            skSolve(sketch);
        }
        {
            var Q0;
            Q0=qSketchRegion(id+"F71",true);
            extrude(context, id + "F72", {"entities" : qUnion([Q0]), "depth" : 10 * mm, "hasSecondDirection" : true, "secondDirectionOppositeDirection" : true, "secondDirectionDepth" : 10 * mm});
        }
        {
            var Q0;
            Q0=qCreatedBy(makeId("Right.planeOp"),FACE);
            var sketch = newSketch(context, id + "F73", { "sketchPlane" : qUnion([Q0])});
            skLineSegment(sketch, "E149.0", {"start": v(215.88, 2953.91) * mm, "end": v(217.07, 2955.98) * mm});
            skLineSegment(sketch, "E150.0", {"start": v(531.66, 2341.91) * mm, "end": v(528.47, 2343.75) * mm});
            skLineSegment(sketch, "E151.0", {"start": v(181.02, 2973.54) * mm, "end": v(182.43, 2975.98) * mm});
            skLineSegment(sketch, "E152.0", {"start": v(-330.77, 2839.84) * mm, "end": v(-333.23, 2841.26) * mm});
            skLineSegment(sketch, "E153.0", {"start": v(-358.23, 2797.96) * mm, "end": v(-355.95, 2796.64) * mm});
            skLineSegment(sketch, "E154", {"start": v(-333.23, 2841.26) * mm, "end": v(182.43, 2975.98) * mm});
            skLineSegment(sketch, "E155", {"start": v(217.07, 2955.98) * mm, "end": v(531.66, 2341.91) * mm});
            skLineSegment(sketch, "E156.0", {"start": v(215.88, 2953.91) * mm, "end": v(528.47, 2343.75) * mm});
            skLineSegment(sketch, "E157.0", {"start": v(-330.77, 2839.84) * mm, "end": v(181.02, 2973.54) * mm});
            skPoint(sketch, "E158.orphan", {"position": v(29.82, 2631.65) * mm});
            skPoint(sketch, "E159.orphan", {"position": v(-4.82, 2651.65) * mm});
            skLineSegment(sketch, "E160", {"start": v(-358.23, 2797.96) * mm, "end": v(0, 913.97) * mm});
            skLineSegment(sketch, "E161.0", {"start": v(-355.95, 2796.64) * mm, "end": v(1.95, 914.4) * mm});
            skPoint(sketch, "E162.orphan", {"position": v(506.66, 2298.6) * mm});
            skLineSegment(sketch, "E163", {"start": v(0, 913.97) * mm, "end": v(1.95, 914.4) * mm});
            skSolve(sketch);
        }
        {
            var Q0;
            Q0=qSketchRegion(id+"F73",true);
            extrude(context, id + "F74", {"entities" : qUnion([Q0]), "depth" : 1 * mm, "hasSecondDirection" : true, "secondDirectionOppositeDirection" : true, "secondDirectionDepth" : 1 * mm});
        }
        {
            var Q0;
            Q0=qCreatedBy(id+"F54.planeOp",FACE);
            var sketch = newSketch(context, id + "F75", { "sketchPlane" : qUnion([Q0])});
            skLineSegment(sketch, "E164.0", {"start": v(-377.63, 740) * mm, "end": v(822.37, 740) * mm});
            skLineSegment(sketch, "E165.0", {"start": v(-301.88, 2817.78) * mm, "end": v(800, 1800) * mm});
            skLineSegment(sketch, "E166", {"start": v(800, 1800) * mm, "end": v(822.37, 740) * mm});
            skLineSegment(sketch, "E167", {"start": v(-301.88, 2817.78) * mm, "end": v(-377.63, 740) * mm});
            skSolve(sketch);
        }
        {
            var Q0;
            Q0 = qSketchRegion(id + "F75", true);
            extrude(context, id + "F76", {"entities" : qUnion([Q0]), "depth" : 1 * mm});
        }
    });
